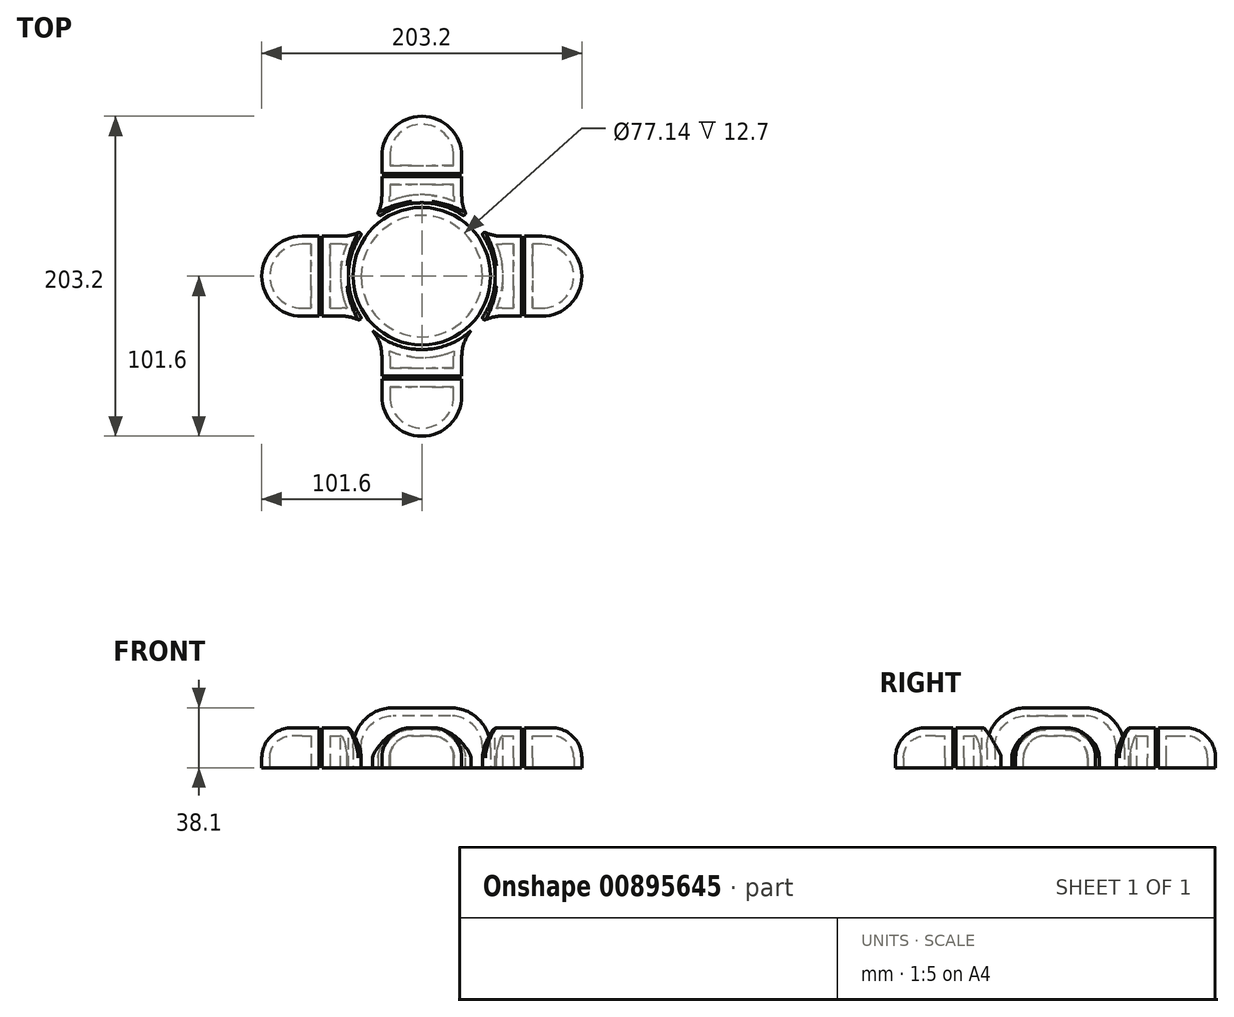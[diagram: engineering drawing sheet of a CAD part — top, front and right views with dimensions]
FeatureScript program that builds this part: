
annotation { "Feature Type Name" : "Feature", "Feature Type Description" : "" }
export const myFeature = defineFeature(function(context is Context, id is Id, definition is map)
    precondition{}
    {
        {
            var Q0;
            Q0=qCreatedBy(makeId("Top.planeOp"),FACE);
            var sketch = newSketch(context, id + "F0", { "sketchPlane" : qUnion([Q0])});
            skLineSegment(sketch, "E0", {"start": v(-101.6, 0) * mm, "end": v(-101.6, 0) * mm});
            skLineSegment(sketch, "E1", {"start": v(-76.2, -25.4) * mm, "end": v(-50.8, -25.4) * mm});
            skLineSegment(sketch, "E2", {"start": v(-25.4, -50.8) * mm, "end": v(-25.4, -76.2) * mm});
            skLineSegment(sketch, "E3", {"start": v(0, -101.6) * mm, "end": v(0, -101.6) * mm});
            skLineSegment(sketch, "E4", {"start": v(25.4, -76.2) * mm, "end": v(25.4, -50.8) * mm});
            skLineSegment(sketch, "E5", {"start": v(50.8, -25.4) * mm, "end": v(76.2, -25.4) * mm});
            skLineSegment(sketch, "E6", {"start": v(101.6, 0) * mm, "end": v(101.6, 0) * mm});
            skLineSegment(sketch, "E7", {"start": v(76.2, 25.4) * mm, "end": v(50.8, 25.4) * mm});
            skLineSegment(sketch, "E8", {"start": v(25.4, 50.8) * mm, "end": v(25.4, 76.2) * mm});
            skLineSegment(sketch, "E9", {"start": v(0, 101.6) * mm, "end": v(0, 101.6) * mm});
            skLineSegment(sketch, "E10", {"start": v(-25.4, 76.2) * mm, "end": v(-25.4, 50.8) * mm});
            skLineSegment(sketch, "E11", {"start": v(-50.8, 25.4) * mm, "end": v(-76.2, 25.4) * mm});
            skPoint(sketch, "E12.visualSharp", {"position": v(-25.4, 25.4) * mm});
            skArc(sketch, "E12.filletArc", {"start": v(-50.8, 25.4) * mm, "mid": v(-32.84, 32.84) * mm, "end": v(-25.4, 50.8) * mm});
            skPoint(sketch, "E13.visualSharp", {"position": v(25.4, 25.4) * mm});
            skArc(sketch, "E13.filletArc", {"start": v(25.4, 50.8) * mm, "mid": v(32.84, 32.84) * mm, "end": v(50.8, 25.4) * mm});
            skPoint(sketch, "E14.visualSharp", {"position": v(25.4, -25.4) * mm});
            skArc(sketch, "E14.filletArc", {"start": v(50.8, -25.4) * mm, "mid": v(32.84, -32.84) * mm, "end": v(25.4, -50.8) * mm});
            skPoint(sketch, "E15.visualSharp", {"position": v(-25.4, -25.4) * mm});
            skArc(sketch, "E15.filletArc", {"start": v(-25.4, -50.8) * mm, "mid": v(-32.84, -32.84) * mm, "end": v(-50.8, -25.4) * mm});
            skPoint(sketch, "E16.visualSharp", {"position": v(-101.6, -25.4) * mm});
            skArc(sketch, "E16.filletArc", {"start": v(-101.6, 0) * mm, "mid": v(-94.16, -17.96) * mm, "end": v(-76.2, -25.4) * mm});
            skPoint(sketch, "E17.visualSharp", {"position": v(-101.6, 25.4) * mm});
            skArc(sketch, "E17.filletArc", {"start": v(-76.2, 25.4) * mm, "mid": v(-94.16, 17.96) * mm, "end": v(-101.6, 0) * mm});
            skPoint(sketch, "E18.visualSharp", {"position": v(-25.4, 101.6) * mm});
            skArc(sketch, "E18.filletArc", {"start": v(0, 101.6) * mm, "mid": v(-17.96, 94.16) * mm, "end": v(-25.4, 76.2) * mm});
            skPoint(sketch, "E19.visualSharp", {"position": v(25.4, 101.6) * mm});
            skArc(sketch, "E19.filletArc", {"start": v(25.4, 76.2) * mm, "mid": v(17.96, 94.16) * mm, "end": v(0, 101.6) * mm});
            skPoint(sketch, "E20.visualSharp", {"position": v(101.6, 25.4) * mm});
            skArc(sketch, "E20.filletArc", {"start": v(101.6, 0) * mm, "mid": v(94.16, 17.96) * mm, "end": v(76.2, 25.4) * mm});
            skPoint(sketch, "E21.visualSharp", {"position": v(101.6, -25.4) * mm});
            skArc(sketch, "E21.filletArc", {"start": v(76.2, -25.4) * mm, "mid": v(94.16, -17.96) * mm, "end": v(101.6, 0) * mm});
            skPoint(sketch, "E22.visualSharp", {"position": v(25.4, -101.6) * mm});
            skArc(sketch, "E22.filletArc", {"start": v(0, -101.6) * mm, "mid": v(17.96, -94.16) * mm, "end": v(25.4, -76.2) * mm});
            skPoint(sketch, "E23.visualSharp", {"position": v(-25.4, -101.6) * mm});
            skArc(sketch, "E23.filletArc", {"start": v(-25.4, -76.2) * mm, "mid": v(-17.96, -94.16) * mm, "end": v(0, -101.6) * mm});
            skSolve(sketch);
        }
        {
            var Q0;
            Q0=makeQuery(id+"F0.imprint","IMPRINT",FACE,{"disambiguationData":[TD([[makeQuery(id+"F0.imprint","IMPRINT",EDGE,{"derivedFrom":sQuery(id+"F0.wireOp",EDGE,"E1")}),1.0]])]});
            extrude(context, id + "F1", {"entities" : qUnion([Q0]), "depth" : 25.4 * mm, "offsetDistance" : 25.4 * mm});
        }
        {
            var Q0;
            Q0=makeQuery(id+"F1.opExtrude","CAP_FACE",FACE,{"disambiguationData":[OSD([sQuery(id+"F0.wireOp",EDGE,"E1"),sQuery(id+"F0.wireOp",EDGE,"E2"),sQuery(id+"F0.wireOp",EDGE,"E4"),sQuery(id+"F0.wireOp",EDGE,"E5"),sQuery(id+"F0.wireOp",EDGE,"E7"),sQuery(id+"F0.wireOp",EDGE,"E8"),sQuery(id+"F0.wireOp",EDGE,"E10"),sQuery(id+"F0.wireOp",EDGE,"E11"),sQuery(id+"F0.wireOp",EDGE,"E12.filletArc"),sQuery(id+"F0.wireOp",EDGE,"E13.filletArc"),sQuery(id+"F0.wireOp",EDGE,"E14.filletArc"),sQuery(id+"F0.wireOp",EDGE,"E15.filletArc"),sQuery(id+"F0.wireOp",EDGE,"E16.filletArc"),sQuery(id+"F0.wireOp",EDGE,"E17.filletArc"),sQuery(id+"F0.wireOp",EDGE,"E18.filletArc"),sQuery(id+"F0.wireOp",EDGE,"E19.filletArc"),sQuery(id+"F0.wireOp",EDGE,"E20.filletArc"),sQuery(id+"F0.wireOp",EDGE,"E21.filletArc"),sQuery(id+"F0.wireOp",EDGE,"E22.filletArc"),sQuery(id+"F0.wireOp",EDGE,"E23.filletArc")])],"isStart":false});
            fillet(context, id + "F2", {"entities" : qUnion([Q0]), "radius" : 19.05 * mm, "tangentPropagation" : true, "allowEdgeOverflow" : false});
        }
        {
            var Q0;
            Q0=makeQuery(id+"F1.opExtrude","CAP_FACE",FACE,{"disambiguationData":[OSD([sQuery(id+"F0.wireOp",EDGE,"E1"),sQuery(id+"F0.wireOp",EDGE,"E2"),sQuery(id+"F0.wireOp",EDGE,"E4"),sQuery(id+"F0.wireOp",EDGE,"E5"),sQuery(id+"F0.wireOp",EDGE,"E7"),sQuery(id+"F0.wireOp",EDGE,"E8"),sQuery(id+"F0.wireOp",EDGE,"E10"),sQuery(id+"F0.wireOp",EDGE,"E11"),sQuery(id+"F0.wireOp",EDGE,"E12.filletArc"),sQuery(id+"F0.wireOp",EDGE,"E13.filletArc"),sQuery(id+"F0.wireOp",EDGE,"E14.filletArc"),sQuery(id+"F0.wireOp",EDGE,"E15.filletArc"),sQuery(id+"F0.wireOp",EDGE,"E16.filletArc"),sQuery(id+"F0.wireOp",EDGE,"E17.filletArc"),sQuery(id+"F0.wireOp",EDGE,"E18.filletArc"),sQuery(id+"F0.wireOp",EDGE,"E19.filletArc"),sQuery(id+"F0.wireOp",EDGE,"E20.filletArc"),sQuery(id+"F0.wireOp",EDGE,"E21.filletArc"),sQuery(id+"F0.wireOp",EDGE,"E22.filletArc"),sQuery(id+"F0.wireOp",EDGE,"E23.filletArc")])],"isStart":false});
            var sketch = newSketch(context, id + "F3", { "sketchPlane" : qUnion([Q0])});
            skCircle(sketch, "E24", {"center": v(0, 0) * mm, "radius": 46.6 * mm});
            skSolve(sketch);
        }
        {
            var Q0;
            Q0 = qSketchRegion(id + "F3", true);
            extrude(context, id + "F4", {"entities" : qUnion([Q0]), "operationType" : NewBodyOperationType.REMOVE, "oppositeDirection" : true, "depth" : 71.12 * mm, "offsetDistance" : 25.4 * mm});
        }
        {
            var Q0;
            Q0=qCreatedBy(makeId("Top.planeOp"),FACE);
            var sketch = newSketch(context, id + "F5", { "sketchPlane" : qUnion([Q0])});
            skCircle(sketch, "E25", {"center": v(0, 0) * mm, "radius": 43.65 * mm});
            skSolve(sketch);
        }
        {
            var Q0;
            Q0=makeQuery(id+"F5.imprint","IMPRINT",FACE,{"disambiguationData":[TD([[makeQuery(id+"F5.imprint","IMPRINT",EDGE,{"derivedFrom":sQuery(id+"F5.wireOp",EDGE,"E25")}),1.0]])]});
            extrude(context, id + "F6", {"entities" : qUnion([Q0]), "depth" : 38.1 * mm, "offsetDistance" : 25.4 * mm});
        }
        {
            var Q0;
            Q0=makeQuery(id+"F6.opExtrude","CAP_EDGE",EDGE,{"disambiguationData":[OSD([sQuery(id+"F5.wireOp",EDGE,"E25")])],"isStart":false});
            fillet(context, id + "F7", {"entities" : qUnion([Q0]), "radius" : 25.4 * mm, "tangentPropagation" : true, "allowEdgeOverflow" : false});
        }
        {
            var Q0;
            Q0=makeQuery(id+"F4.boolean.opBoolean","INTERSECT",EDGE,{"disambiguationData":[OD(0.0)],"derivedFrom":[makeQuery(id+"F2.opFillet","BLEND_FACE",FACE,{"disambiguationData":[OSD([sQuery(id+"F0.wireOp",EDGE,"E13.filletArc")])]}),makeQuery(id+"F4.opExtrude","SWEPT_FACE",FACE,{"disambiguationData":[OSD([sQuery(id+"F3.wireOp",EDGE,"E24")])]})]});
            var Q1;
            Q1=makeQuery(id+"F4.boolean.opBoolean","INTERSECT",EDGE,{"disambiguationData":[OD(0.0)],"derivedFrom":[makeQuery(id+"F2.opFillet","BLEND_FACE",FACE,{"disambiguationData":[OSD([sQuery(id+"F0.wireOp",EDGE,"E14.filletArc")])]}),makeQuery(id+"F4.opExtrude","SWEPT_FACE",FACE,{"disambiguationData":[OSD([sQuery(id+"F3.wireOp",EDGE,"E24")])]})]});
            var Q2;
            {var subQ0=sQuery(id+"F0.wireOp",EDGE,"E15.filletArc");var subQ1=sQuery(id+"F0.wireOp",EDGE,"E12.filletArc");var subQ2=sQuery(id+"F3.wireOp",EDGE,"E24");Q2=makeQuery(id+"F4.boolean.opBoolean","COPY",EDGE,{"disambiguationData":[TD([makeQuery(id+"F1.opExtrude","CAP_FACE",FACE,{"disambiguationData":[OSD([sQuery(id+"F0.wireOp",EDGE,"E1"),sQuery(id+"F0.wireOp",EDGE,"E2"),sQuery(id+"F0.wireOp",EDGE,"E4"),sQuery(id+"F0.wireOp",EDGE,"E5"),sQuery(id+"F0.wireOp",EDGE,"E7"),sQuery(id+"F0.wireOp",EDGE,"E8"),sQuery(id+"F0.wireOp",EDGE,"E10"),sQuery(id+"F0.wireOp",EDGE,"E11"),subQ1,sQuery(id+"F0.wireOp",EDGE,"E13.filletArc"),sQuery(id+"F0.wireOp",EDGE,"E14.filletArc"),subQ0,sQuery(id+"F0.wireOp",EDGE,"E16.filletArc"),sQuery(id+"F0.wireOp",EDGE,"E17.filletArc"),sQuery(id+"F0.wireOp",EDGE,"E18.filletArc"),sQuery(id+"F0.wireOp",EDGE,"E19.filletArc"),sQuery(id+"F0.wireOp",EDGE,"E20.filletArc"),sQuery(id+"F0.wireOp",EDGE,"E21.filletArc"),sQuery(id+"F0.wireOp",EDGE,"E22.filletArc"),sQuery(id+"F0.wireOp",EDGE,"E23.filletArc")])],"isStart":false}),makeQuery(id+"F2.opFillet","BLEND_FACE",FACE,{"disambiguationData":[OSD([subQ1])]}),makeQuery(id+"F2.opFillet","BLEND_FACE",FACE,{"disambiguationData":[OSD([subQ0])]}),makeQuery(id+"F4.opExtrude","SWEPT_FACE",FACE,{"disambiguationData":[OSD([subQ2])]})])],"derivedFrom":makeQuery(id+"F4.opExtrude","CAP_EDGE",EDGE,{"disambiguationData":[OSD([subQ2])],"isStart":true})});}
            var Q3;
            Q3=makeQuery(id+"F4.boolean.opBoolean","INTERSECT",EDGE,{"disambiguationData":[OD(0.0)],"derivedFrom":[makeQuery(id+"F2.opFillet","BLEND_FACE",FACE,{"disambiguationData":[OSD([sQuery(id+"F0.wireOp",EDGE,"E12.filletArc")])]}),makeQuery(id+"F4.opExtrude","SWEPT_FACE",FACE,{"disambiguationData":[OSD([sQuery(id+"F3.wireOp",EDGE,"E24")])]})]});
            fillet(context, id + "F8", {"entities" : qUnion([Q0, Q1, Q2, Q3]), "radius" : 1.27 * mm, "tangentPropagation" : true, "allowEdgeOverflow" : false});
        }
        {
            var Q0;
            Q0=qCreatedBy(makeId("Top.planeOp"),FACE);
            var sketch = newSketch(context, id + "F9", { "sketchPlane" : qUnion([Q0])});
            skLineSegment(sketch, "E26", {"start": v(-65.3, 29.74) * mm, "end": v(-65.3, -30.7) * mm});
            skLineSegment(sketch, "E27", {"start": v(-65.3, -30.7) * mm, "end": v(-63.4, -30.7) * mm});
            skLineSegment(sketch, "E28", {"start": v(-63.4, -30.7) * mm, "end": v(-63.4, 29.74) * mm});
            skLineSegment(sketch, "E29", {"start": v(-63.4, 29.74) * mm, "end": v(-65.3, 29.74) * mm});
            skLineSegment(sketch, "E30.1.0", {"start": v(-29.74, -65.3) * mm, "end": v(30.7, -65.3) * mm});
            skLineSegment(sketch, "E30.1.1", {"start": v(30.7, -63.4) * mm, "end": v(-29.74, -63.4) * mm});
            skLineSegment(sketch, "E30.1.2", {"start": v(-29.74, -63.4) * mm, "end": v(-29.74, -65.3) * mm});
            skLineSegment(sketch, "E30.1.3", {"start": v(30.7, -65.3) * mm, "end": v(30.7, -63.4) * mm});
            skLineSegment(sketch, "E30.2.0", {"start": v(65.3, -29.74) * mm, "end": v(65.3, 30.7) * mm});
            skLineSegment(sketch, "E30.2.1", {"start": v(63.4, 30.7) * mm, "end": v(63.4, -29.74) * mm});
            skLineSegment(sketch, "E30.2.2", {"start": v(63.4, -29.74) * mm, "end": v(65.3, -29.74) * mm});
            skLineSegment(sketch, "E30.2.3", {"start": v(65.3, 30.7) * mm, "end": v(63.4, 30.7) * mm});
            skLineSegment(sketch, "E30.3.0", {"start": v(29.74, 65.3) * mm, "end": v(-30.7, 65.3) * mm});
            skLineSegment(sketch, "E30.3.1", {"start": v(-30.7, 63.4) * mm, "end": v(29.74, 63.4) * mm});
            skLineSegment(sketch, "E30.3.2", {"start": v(29.74, 63.4) * mm, "end": v(29.74, 65.3) * mm});
            skLineSegment(sketch, "E30.3.3", {"start": v(-30.7, 65.3) * mm, "end": v(-30.7, 63.4) * mm});
            skPoint(sketch, "E30.center", {"position": v(0, 0) * mm});
            skSolve(sketch);
        }
        {
            var Q0;
            Q0 = qSketchRegion(id + "F9", true);
            extrude(context, id + "F10", {"entities" : qUnion([Q0]), "operationType" : NewBodyOperationType.REMOVE, "endBound" : BoundingType.SYMMETRIC, "depth" : 69.1 * mm, "offsetDistance" : 25.4 * mm});
        }
        {
            var Q0;
            {var subQ0=sQuery(id+"F0.wireOp",EDGE,"E15.filletArc");var subQ1=sQuery(id+"F0.wireOp",EDGE,"E11");var subQ2=sQuery(id+"F0.wireOp",EDGE,"E12.filletArc");var subQ3=sQuery(id+"F0.wireOp",EDGE,"E1");var subQ4=sQuery(id+"F0.wireOp",EDGE,"E17.filletArc");var subQ5=sQuery(id+"F0.wireOp",EDGE,"E16.filletArc");Q0=makeQuery(id+"F4.boolean.opBoolean","SPLIT",FACE,{"disambiguationData":[TD([makeQuery(id+"F1.opExtrude","SWEPT_FACE",FACE,{"disambiguationData":[OSD([subQ3])]})])],"derivedFrom":makeQuery(id+"F1.opExtrude","CAP_FACE",FACE,{"disambiguationData":[OSD([subQ3,sQuery(id+"F0.wireOp",EDGE,"E2"),sQuery(id+"F0.wireOp",EDGE,"E4"),sQuery(id+"F0.wireOp",EDGE,"E5"),sQuery(id+"F0.wireOp",EDGE,"E7"),sQuery(id+"F0.wireOp",EDGE,"E8"),sQuery(id+"F0.wireOp",EDGE,"E10"),subQ1,subQ2,sQuery(id+"F0.wireOp",EDGE,"E13.filletArc"),sQuery(id+"F0.wireOp",EDGE,"E14.filletArc"),subQ0,subQ5,subQ4,sQuery(id+"F0.wireOp",EDGE,"E18.filletArc"),sQuery(id+"F0.wireOp",EDGE,"E19.filletArc"),sQuery(id+"F0.wireOp",EDGE,"E20.filletArc"),sQuery(id+"F0.wireOp",EDGE,"E21.filletArc"),sQuery(id+"F0.wireOp",EDGE,"E22.filletArc"),sQuery(id+"F0.wireOp",EDGE,"E23.filletArc")])],"isStart":true})});}
            var Q1;
            {var subQ0=sQuery(id+"F0.wireOp",EDGE,"E14.filletArc");var subQ1=sQuery(id+"F0.wireOp",EDGE,"E4");var subQ2=sQuery(id+"F0.wireOp",EDGE,"E15.filletArc");var subQ3=sQuery(id+"F0.wireOp",EDGE,"E2");var subQ4=sQuery(id+"F0.wireOp",EDGE,"E23.filletArc");var subQ5=sQuery(id+"F0.wireOp",EDGE,"E22.filletArc");Q1=makeQuery(id+"F4.boolean.opBoolean","SPLIT",FACE,{"disambiguationData":[TD([makeQuery(id+"F1.opExtrude","SWEPT_FACE",FACE,{"disambiguationData":[OSD([subQ3])]})])],"derivedFrom":makeQuery(id+"F1.opExtrude","CAP_FACE",FACE,{"disambiguationData":[OSD([sQuery(id+"F0.wireOp",EDGE,"E1"),subQ3,subQ1,sQuery(id+"F0.wireOp",EDGE,"E5"),sQuery(id+"F0.wireOp",EDGE,"E7"),sQuery(id+"F0.wireOp",EDGE,"E8"),sQuery(id+"F0.wireOp",EDGE,"E10"),sQuery(id+"F0.wireOp",EDGE,"E11"),sQuery(id+"F0.wireOp",EDGE,"E12.filletArc"),sQuery(id+"F0.wireOp",EDGE,"E13.filletArc"),subQ0,subQ2,sQuery(id+"F0.wireOp",EDGE,"E16.filletArc"),sQuery(id+"F0.wireOp",EDGE,"E17.filletArc"),sQuery(id+"F0.wireOp",EDGE,"E18.filletArc"),sQuery(id+"F0.wireOp",EDGE,"E19.filletArc"),sQuery(id+"F0.wireOp",EDGE,"E20.filletArc"),sQuery(id+"F0.wireOp",EDGE,"E21.filletArc"),subQ5,subQ4])],"isStart":true})});}
            var Q2;
            {var subQ0=sQuery(id+"F0.wireOp",EDGE,"E14.filletArc");var subQ1=sQuery(id+"F0.wireOp",EDGE,"E13.filletArc");var subQ2=sQuery(id+"F0.wireOp",EDGE,"E7");var subQ3=sQuery(id+"F0.wireOp",EDGE,"E5");var subQ4=sQuery(id+"F0.wireOp",EDGE,"E21.filletArc");var subQ5=sQuery(id+"F0.wireOp",EDGE,"E20.filletArc");Q2=makeQuery(id+"F4.boolean.opBoolean","SPLIT",FACE,{"disambiguationData":[TD([makeQuery(id+"F1.opExtrude","SWEPT_FACE",FACE,{"disambiguationData":[OSD([subQ3])]})])],"derivedFrom":makeQuery(id+"F1.opExtrude","CAP_FACE",FACE,{"disambiguationData":[OSD([sQuery(id+"F0.wireOp",EDGE,"E1"),sQuery(id+"F0.wireOp",EDGE,"E2"),sQuery(id+"F0.wireOp",EDGE,"E4"),subQ3,subQ2,sQuery(id+"F0.wireOp",EDGE,"E8"),sQuery(id+"F0.wireOp",EDGE,"E10"),sQuery(id+"F0.wireOp",EDGE,"E11"),sQuery(id+"F0.wireOp",EDGE,"E12.filletArc"),subQ1,subQ0,sQuery(id+"F0.wireOp",EDGE,"E15.filletArc"),sQuery(id+"F0.wireOp",EDGE,"E16.filletArc"),sQuery(id+"F0.wireOp",EDGE,"E17.filletArc"),sQuery(id+"F0.wireOp",EDGE,"E18.filletArc"),sQuery(id+"F0.wireOp",EDGE,"E19.filletArc"),subQ5,subQ4,sQuery(id+"F0.wireOp",EDGE,"E22.filletArc"),sQuery(id+"F0.wireOp",EDGE,"E23.filletArc")])],"isStart":true})});}
            var Q3;
            {var subQ0=sQuery(id+"F0.wireOp",EDGE,"E13.filletArc");var subQ1=sQuery(id+"F0.wireOp",EDGE,"E12.filletArc");var subQ2=sQuery(id+"F0.wireOp",EDGE,"E10");var subQ3=sQuery(id+"F0.wireOp",EDGE,"E8");var subQ4=sQuery(id+"F0.wireOp",EDGE,"E19.filletArc");var subQ5=sQuery(id+"F0.wireOp",EDGE,"E18.filletArc");Q3=makeQuery(id+"F4.boolean.opBoolean","SPLIT",FACE,{"disambiguationData":[TD([makeQuery(id+"F1.opExtrude","SWEPT_FACE",FACE,{"disambiguationData":[OSD([subQ3])]})])],"derivedFrom":makeQuery(id+"F1.opExtrude","CAP_FACE",FACE,{"disambiguationData":[OSD([sQuery(id+"F0.wireOp",EDGE,"E1"),sQuery(id+"F0.wireOp",EDGE,"E2"),sQuery(id+"F0.wireOp",EDGE,"E4"),sQuery(id+"F0.wireOp",EDGE,"E5"),sQuery(id+"F0.wireOp",EDGE,"E7"),subQ3,subQ2,sQuery(id+"F0.wireOp",EDGE,"E11"),subQ1,subQ0,sQuery(id+"F0.wireOp",EDGE,"E14.filletArc"),sQuery(id+"F0.wireOp",EDGE,"E15.filletArc"),sQuery(id+"F0.wireOp",EDGE,"E16.filletArc"),sQuery(id+"F0.wireOp",EDGE,"E17.filletArc"),subQ5,subQ4,sQuery(id+"F0.wireOp",EDGE,"E20.filletArc"),sQuery(id+"F0.wireOp",EDGE,"E21.filletArc"),sQuery(id+"F0.wireOp",EDGE,"E22.filletArc"),sQuery(id+"F0.wireOp",EDGE,"E23.filletArc")])],"isStart":true})});}
            var Q4;
            Q4=makeQuery(id+"F6.opExtrude","CAP_FACE",FACE,{"disambiguationData":[OSD([sQuery(id+"F5.wireOp",EDGE,"E25")])],"isStart":true});
            shell(context, id + "F11", {"entities" : qUnion([Q0, Q1, Q2, Q3, Q4]), "thickness" : 5.08 * mm});
        }
    });
